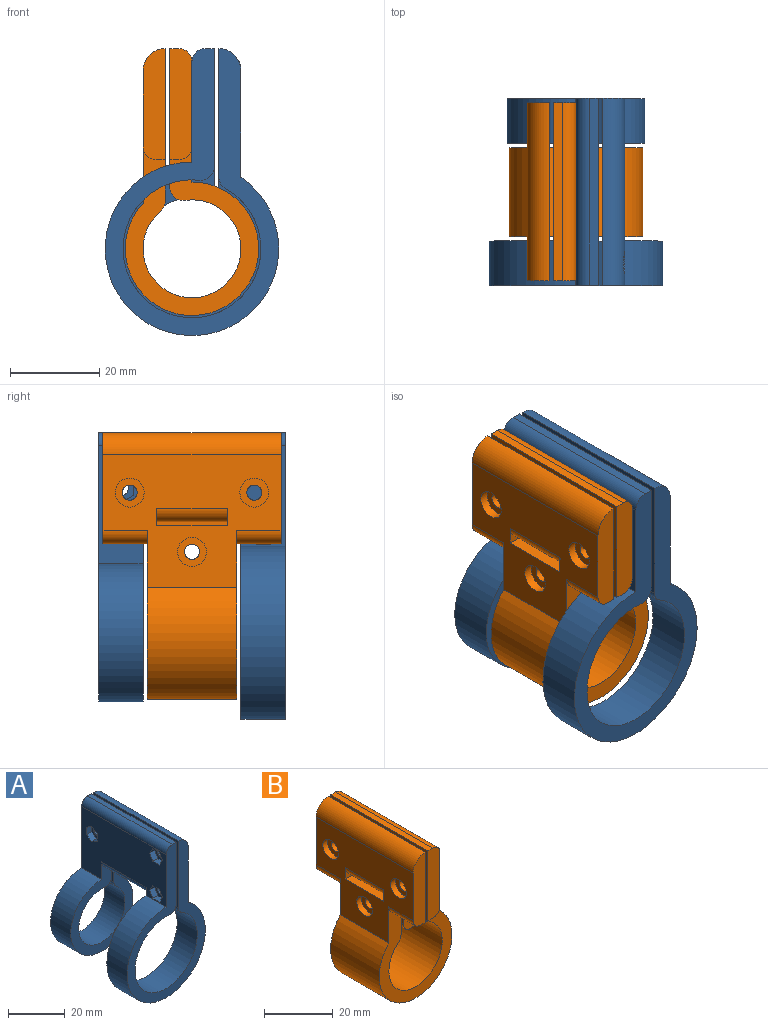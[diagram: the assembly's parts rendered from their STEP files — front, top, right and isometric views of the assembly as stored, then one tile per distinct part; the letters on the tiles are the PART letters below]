
ASSEMBLY  parts=2 mates=1
PART A: 61 faces, bbox 39x42x64.5 mm
  f0: plane 42x29.08mm, normal (1,0,0), area 748.9mm2, adj f1,f3,f6,f9,f12,f13,f15,f16
  f1: cylinder r=5mm len=42mm, axis (0,-1,0), area 321mm2, adj f0,f7,f9,f15,f54
  f2: plane 42x26.5mm, normal (-1,0,0), area 826.5mm2, adj f3,f6,f9,f12,f13,f15,f24,f25
  f3: plane 42.5x39mm, normal (0,1,0), area 452.2mm2, adj f0,f2,f4,f6,f7,f8,f10,f11
  f4: plane 42x30.64mm, normal (1,0,0), area 1095.2mm2, adj f3,f5,f9,f10,f12,f15,f21,f27
  f5: plane 42x2mm, normal (0,0,1), area 84mm2, adj f4,f9,f15,f25
  f6: cylinder r=19.5mm len=39mm, axis (0,1,0), area 1108.3mm2, adj f0,f2,f3,f9
  f7: plane 42x33.63mm, normal (-1,0,0), area 1131.4mm2, adj f1,f3,f9,f11,f12,f15,f16,f17
  f8: cylinder r=15.5mm len=31mm, axis (0,1,0), area 911.9mm2, adj f3,f9,f26,f27
  f9: plane 64.5x39mm, normal (0,-1,0), area 691.1mm2, adj f0,f1,f2,f4,f5,f6,f7,f8
  f10: plane 22x2mm, normal (0,0,-1), area 44mm2, adj f3,f4,f12,f24
  f11: plane 22x2mm, normal (0,0,-1), area 44mm2, adj f3,f7,f12,f23
  f12: plane 38.5x31mm, normal (0,-1,0), area 394.8mm2, adj f0,f2,f4,f7,f10,f11,f13,f14
  f13: cylinder r=15.5mm len=31mm, axis (0,-1,0), area 851.6mm2, adj f0,f2,f12,f15
  f14: cylinder r=11.5mm len=23mm, axis (0,-1,0), area 661.5mm2, adj f12,f15,f21,f22
  f15: plane 60.5x31mm, normal (0,1,0), area 633.6mm2, adj f0,f1,f2,f4,f5,f7,f13,f14
  f16: plane 5x4mm, normal (0,-1,0), area 6.9mm2, adj f0,f7,f17,f18,f20
  f17: plane 16x5mm, normal (0,0,1), area 80mm2, adj f0,f7,f16,f19
  f18: plane 16x2mm, normal (0,0,-1), area 32mm2, adj f7,f16,f19,f20
  f19: plane 5x4mm, normal (0,1,0), area 6.9mm2, adj f0,f7,f17,f18,f20
  f20: cylinder r=3mm len=16mm, axis (0,1,0), area 75.4mm2, adj f0,f16,f18,f19
  f21: cylinder r=3mm len=10mm, axis (0,-1,0), area 51.3mm2, adj f4,f12,f14,f15
  f22: cylinder r=3mm len=10mm, axis (0,-1,0), area 27mm2, adj f7,f12,f14,f15
  f23: cylinder r=3mm len=22mm, axis (0,1,0), area 103.7mm2, adj f0,f3,f11,f12
  f24: cylinder r=3mm len=22mm, axis (0,-1,0), area 103.7mm2, adj f2,f3,f10,f12
  f25: cylinder r=3mm len=42mm, axis (0,1,0), area 197.9mm2, adj f2,f5,f9,f15
  f26: cylinder r=3mm len=10mm, axis (0,1,0), area 31.9mm2, adj f3,f7,f8,f9
  f27: cylinder r=3mm len=10mm, axis (0,1,0), area 50.4mm2, adj f3,f4,f8,f9
  f28: plane 2.8x2.5mm, normal (0,-0.87,-0.5), area 8.1mm2, adj f2,f29,f33,f34
  f29: plane 2.8x2.5mm, normal (0,-0.87,0.5), area 8.1mm2, adj f2,f28,f30,f34
  f30: plane 3.23x2.5mm, normal (0,0,1), area 8.1mm2, adj f2,f29,f31,f34
  f31: plane 2.8x2.5mm, normal (0,0.87,0.5), area 8.1mm2, adj f2,f30,f32,f34
  f32: plane 2.8x2.5mm, normal (0,0.87,-0.5), area 8.1mm2, adj f2,f31,f33,f34
  f33: plane 3.23x2.5mm, normal (0,0,-1), area 8.1mm2, adj f2,f28,f32,f34
  f34: plane 6.47x5.6mm, normal (-1,0,0), area 18.1mm2, adj f28,f29,f30,f31,f32,f33,f51
  f35: plane 2.8x2.5mm, normal (0,0.5,-0.87), area 8.1mm2, adj f2,f36,f40,f41
  f36: plane 2.8x2.5mm, normal (0,-0.5,-0.87), area 8.1mm2, adj f2,f35,f37,f41
  f37: plane 3.23x2.5mm, normal (0,-1,0), area 8.1mm2, adj f2,f36,f38,f41
  f38: plane 2.8x2.5mm, normal (0,-0.5,0.87), area 8.1mm2, adj f2,f37,f39,f41
  f39: plane 2.8x2.5mm, normal (0,0.5,0.87), area 8.1mm2, adj f2,f38,f40,f41
  f40: plane 3.23x2.5mm, normal (0,1,0), area 8.1mm2, adj f2,f35,f39,f41
  f41: plane 6.47x5.6mm, normal (-1,0,0), area 18.1mm2, adj f35,f36,f37,f38,f39,f40,f50
  f42: plane 3.23x2.5mm, normal (0,0,1), area 8.1mm2, adj f2,f43,f47,f48
  f43: plane 2.8x2.5mm, normal (0,0.87,0.5), area 8.1mm2, adj f2,f42,f44,f48
  f44: plane 2.8x2.5mm, normal (0,0.87,-0.5), area 8.1mm2, adj f2,f43,f45,f48
  f45: plane 3.23x2.5mm, normal (0,0,-1), area 8.1mm2, adj f2,f44,f46,f48
  f46: plane 2.8x2.5mm, normal (0,-0.87,-0.5), area 8.1mm2, adj f2,f45,f47,f48
  f47: plane 2.8x2.5mm, normal (0,-0.87,0.5), area 8.1mm2, adj f2,f42,f46,f48
  f48: plane 6.47x5.6mm, normal (-1,0,0), area 18.1mm2, adj f42,f43,f44,f45,f46,f47,f49
  f49: cylinder r=1.7mm len=3.4mm, axis (1,0,0), area 26.7mm2, adj f4,f48
  f50: cylinder r=1.7mm len=3.4mm, axis (1,0,0), area 26.7mm2, adj f4,f41
  f51: cylinder r=1.7mm len=3.4mm, axis (1,0,0), area 26.7mm2, adj f4,f34
  f52: cylinder r=1.7mm len=3.4mm, axis (1,0,0), area 32mm2, adj f7,f53
  f53: plane 6.5x6.5mm, normal (1,0,0), area 24.1mm2, adj f52,f54
  f54: cylinder r=3.25mm len=6.5mm, axis (1,0,0), area 39.2mm2, adj f0,f1,f53
  f55: cylinder r=1.7mm len=3.4mm, axis (1,0,0), area 32mm2, adj f7,f56
  f56: plane 6.5x6.5mm, normal (1,0,0), area 24.1mm2, adj f55,f57
  f57: cylinder r=3.25mm len=6.5mm, axis (1,0,0), area 40.8mm2, adj f0,f56
  f58: cylinder r=1.7mm len=3.4mm, axis (1,0,0), area 32mm2, adj f7,f59
  f59: plane 6.5x6.5mm, normal (1,0,0), area 24.1mm2, adj f58,f60
  f60: cylinder r=3.25mm len=6.5mm, axis (1,0,0), area 40.8mm2, adj f0,f59
PART B: 63 faces, bbox 30x40x60 mm
  f0: plane 40x27mm, normal (1,0,0), area 838.5mm2, adj f1,f2,f8,f16,f18,f24,f25,f29
  f1: plane 38x30mm, normal (0,1,0), area 387.8mm2, adj f0,f4,f5,f6,f7,f8,f17,f19
  f2: plane 38x30mm, normal (0,-1,0), area 387.8mm2, adj f0,f4,f5,f6,f7,f8,f13,f15
  f3: plane 40x2mm, normal (0,0,1), area 80mm2, adj f4,f16,f18,f29
  f4: plane 40x31.14mm, normal (-1,0,0), area 1095.6mm2, adj f1,f2,f3,f15,f16,f17,f18,f27
  f5: cylinder r=11mm len=22mm, axis (0,-1,0), area 1260.2mm2, adj f1,f2,f27,f28
  f6: plane 40x34.28mm, normal (1,0,0), area 1142.5mm2, adj f1,f2,f9,f10,f11,f12,f13,f14
  f7: plane 40x29.8mm, normal (-1,0,0), area 773.2mm2, adj f1,f2,f8,f9,f11,f12,f14,f20
  f8: cylinder r=15mm len=30mm, axis (0,-1,0), area 1638mm2, adj f0,f1,f2,f7
  f9: plane 5x4mm, normal (0,-1,0), area 6.9mm2, adj f6,f7,f10,f11,f22
  f10: plane 15.83x2mm, normal (0,0,-1), area 31.7mm2, adj f6,f9,f12,f22
  f11: plane 15.83x5mm, normal (0,0,1), area 79.2mm2, adj f6,f7,f9,f12
  f12: plane 5x4mm, normal (0,1,0), area 6.9mm2, adj f6,f7,f10,f11,f22
  f13: plane 10x2mm, normal (0,0,-1), area 20mm2, adj f2,f6,f14,f26
  f14: plane 25x5mm, normal (0,-1,0), area 117.7mm2, adj f6,f7,f13,f21,f26
  f15: plane 10x2mm, normal (0,0,-1), area 20mm2, adj f2,f4,f16,f25
  f16: plane 25x5mm, normal (0,-1,0), area 121.1mm2, adj f0,f3,f4,f15,f25,f29
  f17: plane 10x2mm, normal (0,0,-1), area 20mm2, adj f1,f4,f18,f24
  f18: plane 25x5mm, normal (0,1,0), area 121.1mm2, adj f0,f3,f4,f17,f24,f29
  f19: plane 10x2mm, normal (0,0,-1), area 20mm2, adj f1,f6,f20,f23
  f20: plane 25x5mm, normal (0,1,0), area 117.7mm2, adj f6,f7,f19,f21,f23
  f21: cylinder r=5mm len=40mm, axis (0,-1,0), area 314.2mm2, adj f6,f7,f14,f20
  f22: cylinder r=3mm len=15.83mm, axis (0,1,0), area 74.6mm2, adj f7,f9,f10,f12
  f23: cylinder r=3mm len=10mm, axis (0,-1,0), area 47.1mm2, adj f1,f7,f19,f20
  f24: cylinder r=3mm len=10mm, axis (0,1,0), area 47.1mm2, adj f0,f1,f17,f18
  f25: cylinder r=3mm len=10mm, axis (0,1,0), area 47.1mm2, adj f0,f2,f15,f16
  f26: cylinder r=3mm len=10mm, axis (0,-1,0), area 47.1mm2, adj f2,f7,f13,f14
  f27: cylinder r=3mm len=20mm, axis (0,-1,0), area 102.8mm2, adj f1,f2,f4,f5
  f28: cylinder r=3mm len=20mm, axis (0,-1,0), area 52.4mm2, adj f1,f2,f5,f6
  f29: cylinder r=3mm len=40mm, axis (0,-1,0), area 188.5mm2, adj f0,f3,f16,f18
  f30: plane 2.8x2.5mm, normal (0,0.5,-0.87), area 8.1mm2, adj f0,f31,f35,f36
  f31: plane 3.23x2.5mm, normal (0,1,0), area 8.1mm2, adj f0,f30,f32,f36
  f32: plane 2.8x2.5mm, normal (0,0.5,0.87), area 8.1mm2, adj f0,f31,f33,f36
  f33: plane 2.8x2.5mm, normal (0,-0.5,0.87), area 8.1mm2, adj f0,f32,f34,f36
  f34: plane 3.23x2.5mm, normal (0,-1,0), area 8.1mm2, adj f0,f33,f35,f36
  f35: plane 2.8x2.5mm, normal (0,-0.5,-0.87), area 8.1mm2, adj f0,f30,f34,f36
  f36: plane 6.47x5.6mm, normal (1,0,0), area 18.1mm2, adj f30,f31,f32,f33,f34,f35,f53
  f37: plane 3.23x2.5mm, normal (0,0,-1), area 8.1mm2, adj f0,f38,f42,f43
  f38: plane 2.8x2.5mm, normal (0,0.87,-0.5), area 8.1mm2, adj f0,f37,f39,f43
  f39: plane 2.8x2.5mm, normal (0,0.87,0.5), area 8.1mm2, adj f0,f38,f40,f43
  f40: plane 3.23x2.5mm, normal (0,0,1), area 8.1mm2, adj f0,f39,f41,f43
  f41: plane 2.8x2.5mm, normal (0,-0.87,0.5), area 8.1mm2, adj f0,f40,f42,f43
  f42: plane 2.8x2.5mm, normal (0,-0.87,-0.5), area 8.1mm2, adj f0,f37,f41,f43
  f43: plane 6.47x5.6mm, normal (1,0,0), area 18.1mm2, adj f37,f38,f39,f40,f41,f42,f52
  f44: plane 2.8x2.5mm, normal (0,-0.5,0.87), area 8.1mm2, adj f0,f45,f49,f50
  f45: plane 3.23x2.5mm, normal (0,-1,0), area 8.1mm2, adj f0,f44,f46,f50
  f46: plane 2.8x2.5mm, normal (0,-0.5,-0.87), area 8.1mm2, adj f0,f45,f47,f50
  f47: plane 2.8x2.5mm, normal (0,0.5,-0.87), area 8.1mm2, adj f0,f46,f48,f50
  f48: plane 3.23x2.5mm, normal (0,1,0), area 8.1mm2, adj f0,f47,f49,f50
  f49: plane 2.8x2.5mm, normal (0,0.5,0.87), area 8.1mm2, adj f0,f44,f48,f50
  f50: plane 6.47x5.6mm, normal (1,0,0), area 18.1mm2, adj f44,f45,f46,f47,f48,f49,f51
  f51: cylinder r=1.7mm len=3.4mm, axis (-1,0,0), area 26.7mm2, adj f4,f50
  f52: cylinder r=1.7mm len=3.4mm, axis (-1,0,0), area 26.7mm2, adj f4,f43
  f53: cylinder r=1.7mm len=3.4mm, axis (-1,0,0), area 26.7mm2, adj f4,f36
  f54: cylinder r=1.7mm len=3.4mm, axis (-1,0,0), area 32mm2, adj f6,f55
  f55: plane 6.5x6.5mm, normal (-1,0,0), area 24.1mm2, adj f54,f56
  f56: cylinder r=3.25mm len=6.5mm, axis (-1,0,0), area 40.8mm2, adj f7,f55
  f57: cylinder r=1.7mm len=3.4mm, axis (-1,0,0), area 32mm2, adj f6,f58
  f58: plane 6.5x6.5mm, normal (-1,0,0), area 24.1mm2, adj f57,f59
  f59: cylinder r=3.25mm len=6.5mm, axis (-1,0,0), area 40.8mm2, adj f7,f58
  f60: cylinder r=1.7mm len=3.4mm, axis (-1,0,0), area 32mm2, adj f6,f61
  f61: plane 6.5x6.5mm, normal (-1,0,0), area 24.1mm2, adj f60,f62
  f62: cylinder r=3.25mm len=6.5mm, axis (-1,0,0), area 40.8mm2, adj f7,f61
PLACE A rot(axis=(0,1,0),0deg) t=(0,-1,0)mm
PLACE B at identity fixed
MATE revolute B.f5 <-> A.f8  axis (0,-1,0) through (0,0,0)mm
